annotation { "Feature Type Name" : "Feature", "Feature Type Description" : "" }
export const myFeature = defineFeature(function(context is Context, id is Id, definition is map)
    precondition{}
    {
        {
            var Q0;
            Q0=qCreatedBy(makeId("Top.planeOp"),FACE);
            var sketch = newSketch(context, id + "F0", { "sketchPlane" : qUnion([Q0])});
            skLineSegment(sketch, "E0", {"start": v(-304.8, 1066.8) * mm, "end": v(304.8, 1066.8) * mm});
            skLineSegment(sketch, "E1", {"start": v(0, 1066.8) * mm, "end": v(0, -1066.8) * mm});
            skPoint(sketch, "E1.endSnap0", {"position": v(0, 1066.8) * mm});
            skLineSegment(sketch, "E2", {"start": v(-304.8, 1066.8) * mm, "end": v(-511.64, 407.92) * mm});
            skLineSegment(sketch, "E3", {"start": v(-511.64, 407.92) * mm, "end": v(-304.8, -1066.8) * mm});
            skLineSegment(sketch, "E4", {"start": v(-304.8, -1066.8) * mm, "end": v(0, -1066.8) * mm});
            skLineSegment(sketch, "E5.MirrorCS", {"start": v(304.8, 1066.8) * mm, "end": v(511.64, 407.92) * mm});
            skLineSegment(sketch, "E6.MirrorCS", {"start": v(511.64, 407.92) * mm, "end": v(304.8, -1066.8) * mm});
            skLineSegment(sketch, "E7.MirrorCS", {"start": v(304.8, -1066.8) * mm, "end": v(0, -1066.8) * mm});
            skSolve(sketch);
        }
        {
            var Q0;
            Q0 = qSketchRegion(id + "F0", true);
            extrude(context, id + "F1", {"entities" : qUnion([Q0]), "depth" : 609.6 * mm});
        }
        {
            var Q0;
            Q0=makeQuery(id+"F1.opExtrude","CAP_EDGE",EDGE,{"disambiguationData":[OSD([sQuery(id+"F0.wireOp",EDGE,"E3")])],"isStart":false});
            var Q1;
            Q1=makeQuery(id+"F1.opExtrude","CAP_EDGE",EDGE,{"disambiguationData":[OSD([sQuery(id+"F0.wireOp",EDGE,"E2")])],"isStart":false});
            var Q2;
            Q2=makeQuery(id+"F1.opExtrude","CAP_EDGE",EDGE,{"disambiguationData":[OSD([sQuery(id+"F0.wireOp",EDGE,"E0")])],"isStart":false});
            var Q3;
            Q3=makeQuery(id+"F1.opExtrude","CAP_EDGE",EDGE,{"disambiguationData":[OSD([sQuery(id+"F0.wireOp",EDGE,"E5.MirrorCS")])],"isStart":false});
            var Q4;
            Q4=makeQuery(id+"F1.opExtrude","CAP_EDGE",EDGE,{"disambiguationData":[OSD([sQuery(id+"F0.wireOp",EDGE,"E6.MirrorCS")])],"isStart":false});
            var Q5;
            Q5=makeQuery(id+"F1.opExtrude","CAP_EDGE",EDGE,{"disambiguationData":[OSD([sQuery(id+"F0.wireOp",EDGE,"E4"),sQuery(id+"F0.wireOp",EDGE,"E7.MirrorCS")])],"isStart":false});
            chamfer(context, id + "F2", {"entities" : qUnion([Q0, Q1, Q2, Q3, Q4, Q5]), "width" : 101.6 * mm, "tangentPropagation" : true});
        }
        {
            var Q0;
            Q0=makeQuery(id+"F1.opExtrude","CAP_FACE",FACE,{"disambiguationData":[OSD([sQuery(id+"F0.wireOp",EDGE,"E0"),sQuery(id+"F0.wireOp",EDGE,"E2"),sQuery(id+"F0.wireOp",EDGE,"E3"),sQuery(id+"F0.wireOp",EDGE,"E4"),sQuery(id+"F0.wireOp",EDGE,"E5.MirrorCS"),sQuery(id+"F0.wireOp",EDGE,"E6.MirrorCS"),sQuery(id+"F0.wireOp",EDGE,"E7.MirrorCS")])],"isStart":false});
            var sketch = newSketch(context, id + "F3", { "sketchPlane" : qUnion([Q0])});
            skText(sketch, "E8", { "text": "R. I. P.", "fontName": "OpenSans-Bold.ttf"});
            skText(sketch, "E9", { "text": "Jacob Harmon", "fontName": "OpenSans-Regular.ttf"});
            skText(sketch, "E10", { "text": "Jacob Harmon", "fontName": "OpenSans-Regular.ttf"});
            const initialGuessF3  = {"E8": [-0.3548, 0.39431, 1, 0, 0.1637], "E9": [-0.0116, 0.39306, 1, 0, 0.00125], "E10": [-0.16856, 0.26421, 1, 0, 0.0442]};
            skSetInitialGuess(sketch, initialGuessF3);
            skSolve(sketch);
        }
        {
            var Q0;
            Q0 = qSketchRegion(id + "F3", true);
            extrude(context, id + "F4", {"entities" : qUnion([Q0]), "operationType" : NewBodyOperationType.REMOVE, "oppositeDirection" : true, "depth" : 25.4 * mm});
        }
        {
            var Q0;
            Q0=makeQuery(id+"F1.opExtrude","CAP_FACE",FACE,{"disambiguationData":[OSD([sQuery(id+"F0.wireOp",EDGE,"E0"),sQuery(id+"F0.wireOp",EDGE,"E2"),sQuery(id+"F0.wireOp",EDGE,"E3"),sQuery(id+"F0.wireOp",EDGE,"E4"),sQuery(id+"F0.wireOp",EDGE,"E5.MirrorCS"),sQuery(id+"F0.wireOp",EDGE,"E6.MirrorCS"),sQuery(id+"F0.wireOp",EDGE,"E7.MirrorCS")])],"isStart":true});
            var sketch = newSketch(context, id + "F5", { "sketchPlane" : qUnion([Q0])});
            skLineSegment(sketch, "E11.0", {"start": v(269.37, -1018.54) * mm, "end": v(462.34, -403.85) * mm});
            skLineSegment(sketch, "E11.1", {"start": v(-262.84, 1018.54) * mm, "end": v(262.84, 1018.54) * mm});
            skLineSegment(sketch, "E11.2", {"start": v(-462.34, -403.85) * mm, "end": v(-262.84, 1018.54) * mm});
            skLineSegment(sketch, "E11.3", {"start": v(462.34, -403.85) * mm, "end": v(262.84, 1018.54) * mm});
            skLineSegment(sketch, "E11.4", {"start": v(-269.37, -1018.54) * mm, "end": v(-462.34, -403.85) * mm});
            skLineSegment(sketch, "E11.5", {"start": v(-269.37, -1018.54) * mm, "end": v(269.37, -1018.54) * mm});
            skSolve(sketch);
        }
        {
            var Q0;
            Q0 = qSketchRegion(id + "F5", true);
            extrude(context, id + "F6", {"entities" : qUnion([Q0]), "operationType" : NewBodyOperationType.REMOVE, "oppositeDirection" : true, "depth" : 518.16 * mm});
        }
    });